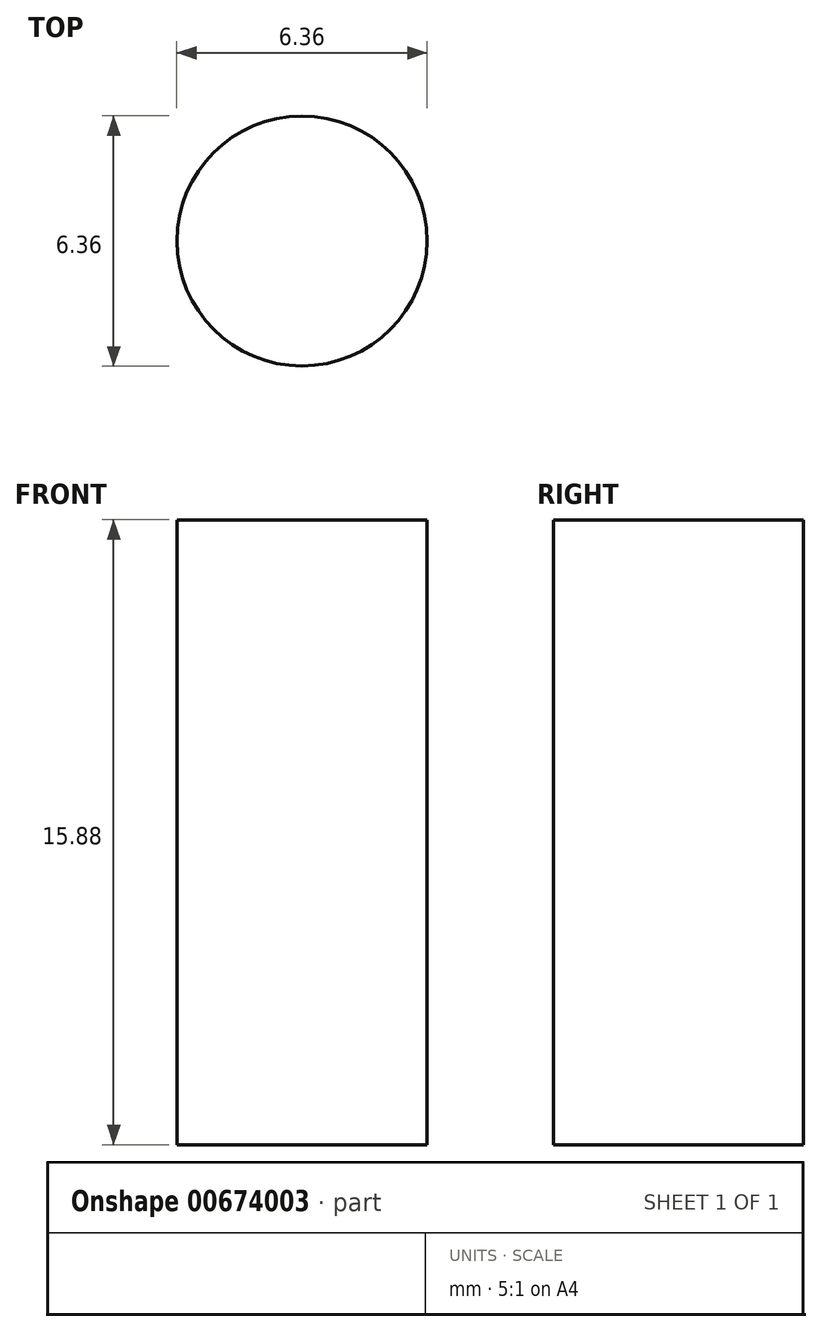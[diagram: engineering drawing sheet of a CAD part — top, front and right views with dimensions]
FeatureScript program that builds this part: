
annotation { "Feature Type Name" : "Feature", "Feature Type Description" : "" }
export const myFeature = defineFeature(function(context is Context, id is Id, definition is map)
    precondition{}
    {
        {
            var Q0;
            Q0=qCreatedBy(makeId("Top.planeOp"),FACE);
            var sketch = newSketch(context, id + "F0", { "sketchPlane" : qUnion([Q0])});
            skCircle(sketch, "E0", {"center": v(0, 0) * mm, "radius": 3.18 * mm});
            skSolve(sketch);
        }
        {
            var Q0;
            Q0=makeQuery(id+"F0.imprint","IMPRINT",FACE,{"disambiguationData":[TD([[makeQuery(id+"F0.imprint","IMPRINT",EDGE,{"derivedFrom":sQuery(id+"F0.wireOp",EDGE,"E0")}),1.0]])]});
            extrude(context, id + "F1", {"entities" : qUnion([Q0]), "depth" : 15.88 * mm, "offsetDistance" : 25.4 * mm});
        }
    });
